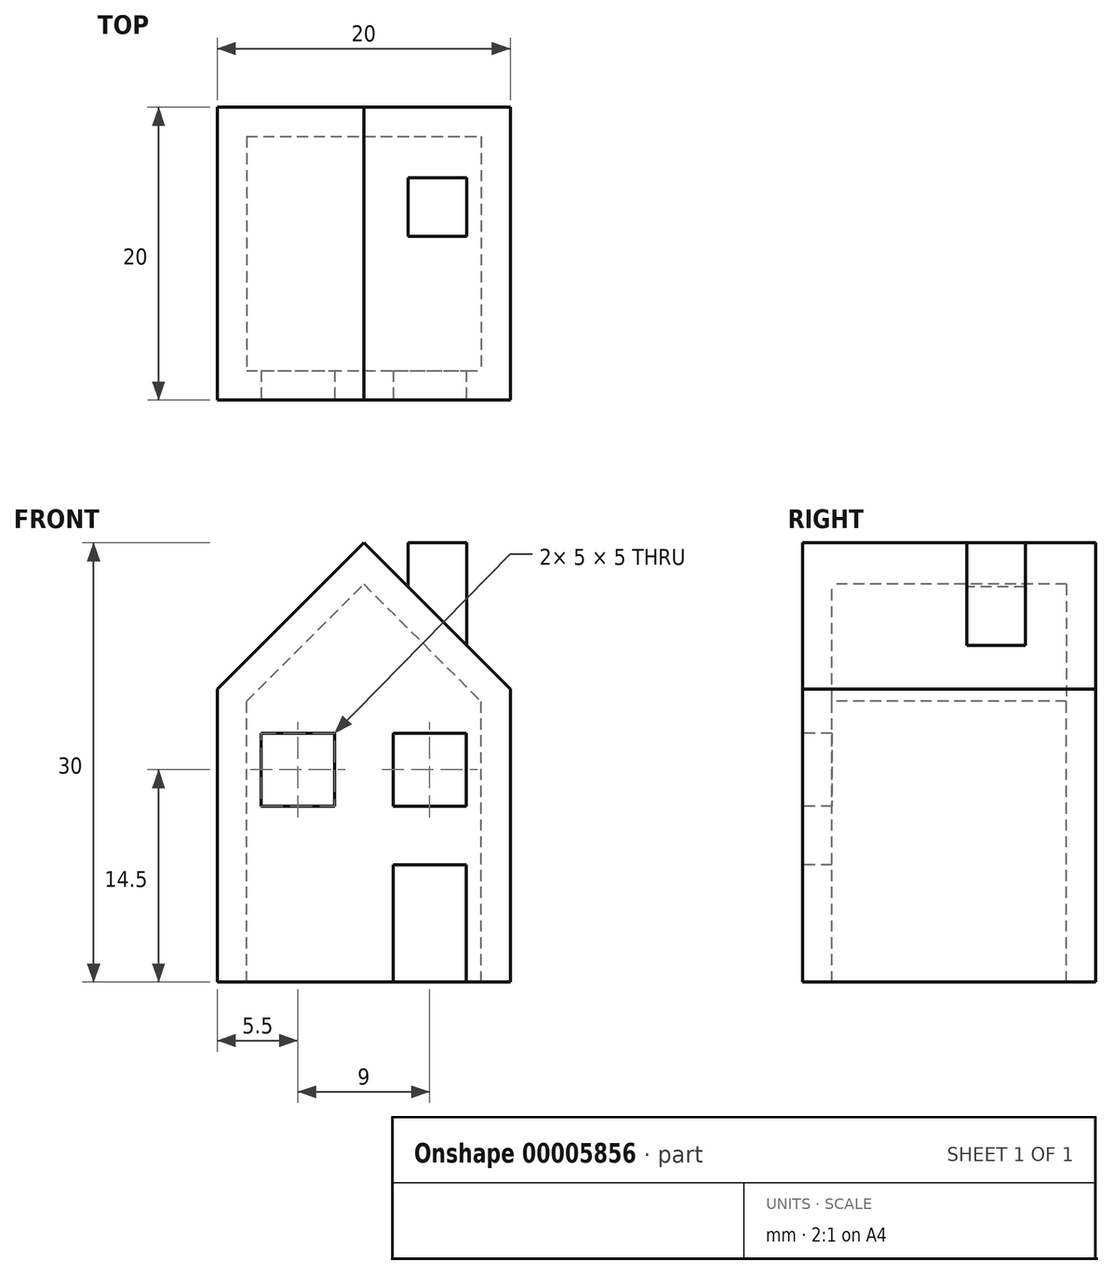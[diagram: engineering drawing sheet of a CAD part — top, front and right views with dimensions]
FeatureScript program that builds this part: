
annotation { "Feature Type Name" : "Feature", "Feature Type Description" : "" }
export const myFeature = defineFeature(function(context is Context, id is Id, definition is map)
    precondition{}
    {
        {
            var Q0;
            Q0=qCreatedBy(makeId("Front.planeOp"),FACE);
            var sketch = newSketch(context, id + "F0", { "sketchPlane" : qUnion([Q0])});
            skLineSegment(sketch, "E0.bottom", {"start": v(0, 0) * mm, "end": v(20, 0) * mm});
            skLineSegment(sketch, "E0.top", {"start": v(0, 20) * mm, "end": v(20, 20) * mm});
            skLineSegment(sketch, "E0.left", {"start": v(0, 0) * mm, "end": v(0, 20) * mm});
            skLineSegment(sketch, "E0.right", {"start": v(20, 0) * mm, "end": v(20, 20) * mm});
            skLineSegment(sketch, "E1", {"start": v(0, 20) * mm, "end": v(10, 30) * mm});
            skLineSegment(sketch, "E2", {"start": v(10, 30) * mm, "end": v(20, 20) * mm});
            skSolve(sketch);
        }
        {
            var Q0;
            Q0=makeQuery(id+"F0.imprint","IMPRINT",FACE,{"disambiguationData":[TD([[makeQuery(id+"F0.imprint","IMPRINT",EDGE,{"derivedFrom":sQuery(id+"F0.wireOp",EDGE,"E0.bottom")}),1.0]])]});
            var Q1;
            Q1=makeQuery(id+"F0.imprint","IMPRINT",FACE,{"disambiguationData":[TD([[makeQuery(id+"F0.imprint","IMPRINT",EDGE,{"derivedFrom":sQuery(id+"F0.wireOp",EDGE,"E0.top")}),1.0]])]});
            extrude(context, id + "F1", {"entities" : qUnion([Q0, Q1]), "oppositeDirection" : true, "depth" : 20 * mm});
        }
        {
            var Q0;
            Q0=makeQuery(id+"F1.opExtrude","SWEPT_FACE",FACE,{"disambiguationData":[OSD([sQuery(id+"F0.wireOp",EDGE,"E0.bottom")])]});
            shell(context, id + "F2", {"entities" : qUnion([Q0]), "thickness" : 2 * mm});
        }
        {
            var Q0;
            Q0=makeQuery(id+"F1.opExtrude","CAP_FACE",FACE,{"disambiguationData":[OSD([sQuery(id+"F0.wireOp",EDGE,"E0.bottom"),sQuery(id+"F0.wireOp",EDGE,"E0.left"),sQuery(id+"F0.wireOp",EDGE,"E0.right"),sQuery(id+"F0.wireOp",EDGE,"E1"),sQuery(id+"F0.wireOp",EDGE,"E2")])],"isStart":true});
            var sketch = newSketch(context, id + "F3", { "sketchPlane" : qUnion([Q0])});
            skLineSegment(sketch, "E3.bottom", {"start": v(12, 0) * mm, "end": v(17, 0) * mm});
            skLineSegment(sketch, "E3.top", {"start": v(12, 8) * mm, "end": v(17, 8) * mm});
            skLineSegment(sketch, "E3.left", {"start": v(12, 0) * mm, "end": v(12, 8) * mm});
            skLineSegment(sketch, "E3.right", {"start": v(17, 0) * mm, "end": v(17, 8) * mm});
            skLineSegment(sketch, "E4.bottom", {"start": v(3, 17) * mm, "end": v(8, 17) * mm});
            skLineSegment(sketch, "E4.top", {"start": v(3, 12) * mm, "end": v(8, 12) * mm});
            skLineSegment(sketch, "E4.left", {"start": v(3, 17) * mm, "end": v(3, 12) * mm});
            skLineSegment(sketch, "E4.right", {"start": v(8, 17) * mm, "end": v(8, 12) * mm});
            skLineSegment(sketch, "E5.bottom", {"start": v(12, 17) * mm, "end": v(17, 17) * mm});
            skLineSegment(sketch, "E5.top", {"start": v(12, 12) * mm, "end": v(17, 12) * mm});
            skLineSegment(sketch, "E5.left", {"start": v(12, 17) * mm, "end": v(12, 12) * mm});
            skLineSegment(sketch, "E5.right", {"start": v(17, 17) * mm, "end": v(17, 12) * mm});
            skSolve(sketch);
        }
        {
            var Q0;
            Q0=makeQuery(id+"F3.imprint","IMPRINT",FACE,{"disambiguationData":[TD([[makeQuery(id+"F3.imprint","IMPRINT",EDGE,{"derivedFrom":sQuery(id+"F3.wireOp",EDGE,"E4.bottom")}),-1.0]])]});
            var Q1;
            Q1=makeQuery(id+"F3.imprint","IMPRINT",FACE,{"disambiguationData":[TD([[makeQuery(id+"F3.imprint","IMPRINT",EDGE,{"derivedFrom":sQuery(id+"F3.wireOp",EDGE,"E5.bottom")}),-1.0]])]});
            var Q2;
            Q2=makeQuery(id+"F3.imprint","IMPRINT",FACE,{"disambiguationData":[TD([[makeQuery(id+"F3.imprint","IMPRINT",EDGE,{"derivedFrom":sQuery(id+"F3.wireOp",EDGE,"E3.bottom")}),1.0]])]});
            var Q3;
            {var subQ0=sQuery(id+"F0.wireOp",EDGE,"E0.bottom");var subQ1=sQuery(id+"F0.wireOp",EDGE,"E0.left");var subQ2=sQuery(id+"F0.wireOp",EDGE,"E0.right");var subQ3=sQuery(id+"F0.wireOp",EDGE,"E1");var subQ4=sQuery(id+"F0.wireOp",EDGE,"E2");Q3=makeQuery(id+"F2.opShell","OFFSET_FACE",FACE,{"disambiguationData":[OSD([subQ0,subQ1,subQ2,subQ3,subQ4]),TDD([makeQuery(id+"F1.opExtrude","CAP_FACE",FACE,{"disambiguationData":[OSD([subQ0,subQ1,subQ2,subQ3,subQ4])],"isStart":false})])]});}
            extrude(context, id + "F4", {"entities" : qUnion([Q0, Q1, Q2]), "operationType" : NewBodyOperationType.REMOVE, "endBound" : BoundingType.UP_TO_SURFACE, "oppositeDirection" : true, "endBoundEntityFace" : qUnion([Q3]), "depth" : 25 * mm});
        }
        {
            var Q0;
            Q0=makeQuery(id+"F1.opExtrude","SWEPT_FACE",FACE,{"disambiguationData":[OSD([sQuery(id+"F0.wireOp",EDGE,"E0.bottom")])]});
            cPlane(context, id + "F5", {"entities" : qUnion([Q0]), "cplaneType" : CPlaneType.OFFSET, "offset" : 30 * mm, "oppositeDirection" : true, "width" : 150 * mm, "height" : 150 * mm});
        }
        {
            var Q0;
            Q0=qCreatedBy(id+"F5.planeOp",FACE);
            var sketch = newSketch(context, id + "F6", { "sketchPlane" : qUnion([Q0])});
            skLineSegment(sketch, "E6.bottom", {"start": v(13.02, -15.19) * mm, "end": v(17.02, -15.19) * mm});
            skLineSegment(sketch, "E6.top", {"start": v(13.02, -11.19) * mm, "end": v(17.02, -11.19) * mm});
            skLineSegment(sketch, "E6.left", {"start": v(13.02, -15.19) * mm, "end": v(13.02, -11.19) * mm});
            skLineSegment(sketch, "E6.right", {"start": v(17.02, -15.19) * mm, "end": v(17.02, -11.19) * mm});
            skSolve(sketch);
        }
        {
            var Q0;
            Q0=makeQuery(id+"F6.imprint","IMPRINT",FACE,{"disambiguationData":[TD([[makeQuery(id+"F6.imprint","IMPRINT",EDGE,{"derivedFrom":sQuery(id+"F6.wireOp",EDGE,"E6.bottom")}),1.0]])]});
            var Q1;
            Q1=makeQuery(id+"F1.opExtrude","SWEPT_FACE",FACE,{"disambiguationData":[OSD([sQuery(id+"F0.wireOp",EDGE,"E2")])]});
            extrude(context, id + "F7", {"entities" : qUnion([Q0]), "operationType" : NewBodyOperationType.ADD, "endBound" : BoundingType.UP_TO_SURFACE, "endBoundEntityFace" : qUnion([Q1]), "depth" : 25 * mm});
        }
    });
